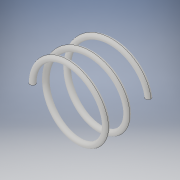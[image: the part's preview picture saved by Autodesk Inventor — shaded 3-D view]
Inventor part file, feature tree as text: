
AUTODESK INVENTOR PART (.ipt)
format: ipt  version: 2019 (Build 230136000, 136)  size: 296,960 bytes
history: native  units: mm
features: helix x1, sketch x1
ambient origin geometry x8: Origin, YZ Plane, XZ Plane, XY Plane, X Axis, Y Axis, Z Axis, Center Point
bodies: Solid1 (feature_tree)
feature tree (2):
  helix  "Coil1"  [1 undecoded]
  sketch  "Sketch1"  dims[d1=3.25mm d2=4.2mm d3=10.0mm d4=4.2mm d5=20.0mm d6=0.0mm d7=90.0deg d8=90.0deg d9=0.0mm d10=0.0mm]
note: 1 required parameter value undecoded (feature->parameter linkage not recoverable at this tier; creation-order binding heuristic only, values carry confidence <= 0.55)
